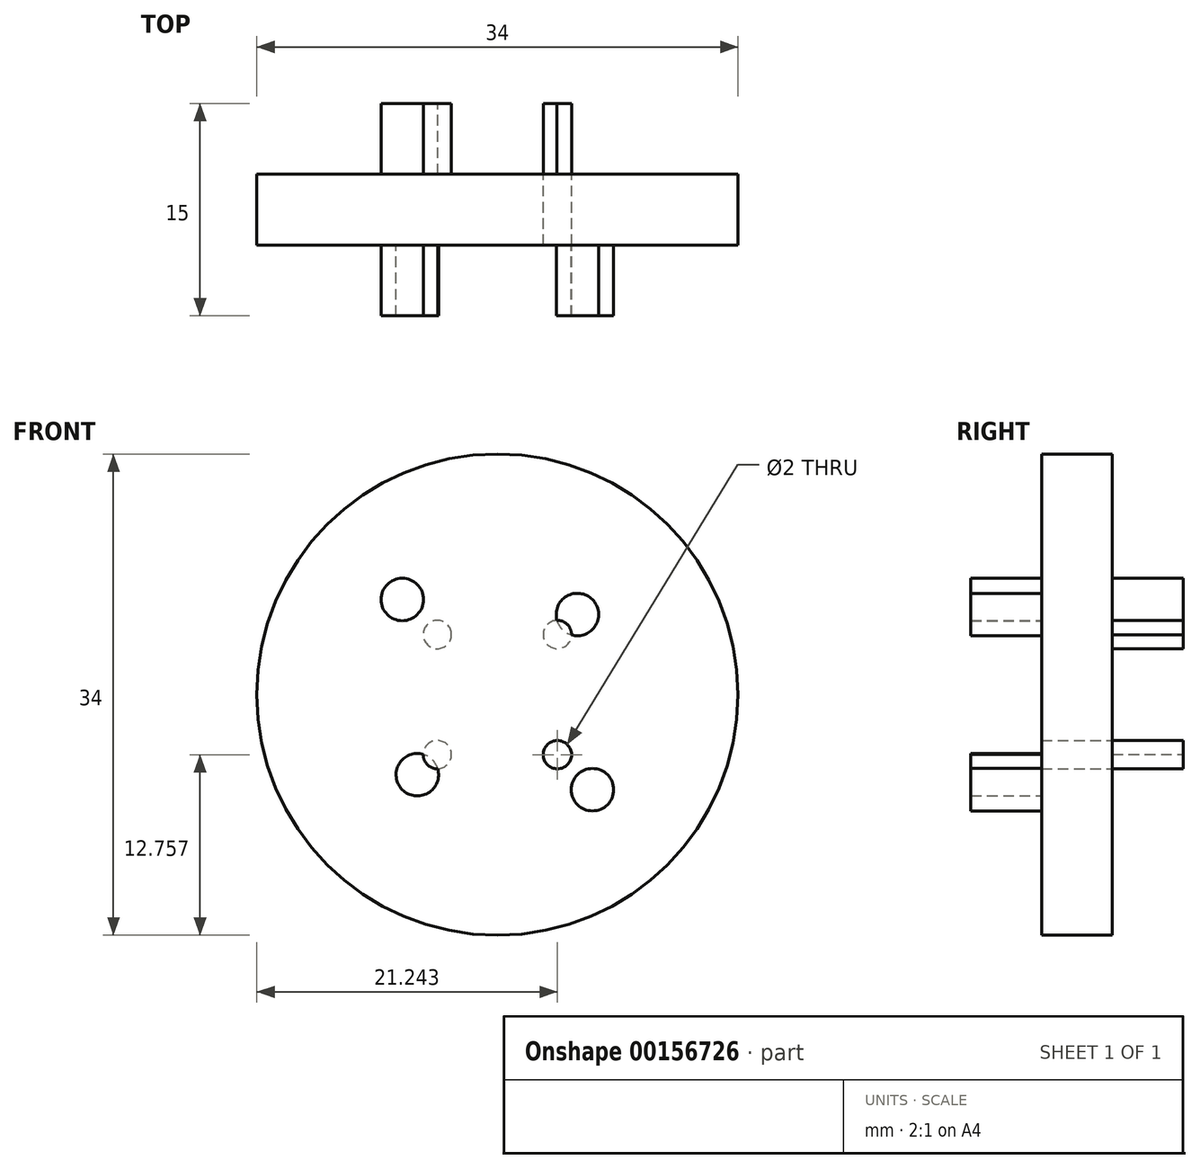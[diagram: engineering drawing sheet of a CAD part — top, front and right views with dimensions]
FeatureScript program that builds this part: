
annotation { "Feature Type Name" : "Feature", "Feature Type Description" : "" }
export const myFeature = defineFeature(function(context is Context, id is Id, definition is map)
    precondition{}
    {
        {
            var Q0;
            Q0=qCreatedBy(makeId("Front.planeOp"),FACE);
            var sketch = newSketch(context, id + "F0", { "sketchPlane" : qUnion([Q0])});
            skCircle(sketch, "E0", {"center": v(0, 0) * mm, "radius": 17 * mm});
            skCircle(sketch, "E1", {"center": v(5.66, 5.66) * mm, "radius": 1.5 * mm});
            skCircle(sketch, "E2.MirrorC", {"center": v(-6.72, 6.72) * mm, "radius": 1.5 * mm});
            skCircle(sketch, "E3.MirrorC", {"center": v(-5.66, -5.66) * mm, "radius": 1.5 * mm});
            skLineSegment(sketch, "E4", {"start": v(0, 29.65) * mm, "end": v(0, -28.8) * mm, "construction": true});
            skLineSegment(sketch, "E5", {"start": v(-6.72, 6.72) * mm, "end": v(4.6, -4.6) * mm, "construction": true});
            skLineSegment(sketch, "E6", {"start": v(5.66, 5.66) * mm, "end": v(-5.66, -5.66) * mm, "construction": true});
            skCircle(sketch, "E7", {"center": v(-4.24, 4.24) * mm, "radius": 1 * mm});
            skCircle(sketch, "E8.MirrorC", {"center": v(4.24, 4.24) * mm, "radius": 1 * mm});
            skCircle(sketch, "E9.MirrorC", {"center": v(4.24, -4.24) * mm, "radius": 1 * mm});
            skCircle(sketch, "E10.MirrorC", {"center": v(-4.24, -4.24) * mm, "radius": 1 * mm});
            skCircle(sketch, "E11.MirrorC", {"center": v(6.72, -6.72) * mm, "radius": 1.5 * mm});
            skSolve(sketch);
        }
        {
            var Q0;
            Q0=makeQuery(id+"F0.imprint","IMPRINT",FACE,{"disambiguationData":[TD([[makeQuery(id+"F0.imprint","IMPRINT",EDGE,{"derivedFrom":sQuery(id+"F0.wireOp",EDGE,"E0")}),1.0]])]});
            var Q1;
            {var subQ0=sQuery(id+"F0.wireOp",EDGE,"E7");var subQ1=sQuery(id+"F0.wireOp",EDGE,"E2.MirrorC");var subQ2=makeQuery(id+"F0.imprint","INTERSECT",VERTEX,{"disambiguationData":[OD(0.0)],"derivedFrom":[subQ1,subQ0]});Q1=makeQuery(id+"F0.imprint","IMPRINT",FACE,{"disambiguationData":[TD([[makeQuery(id+"F0.imprint","IMPRINT",EDGE,{"disambiguationData":[TD([[subQ2,-1.0]])],"derivedFrom":subQ1}),-1.0]])]});}
            var Q2;
            {var subQ0=sQuery(id+"F0.wireOp",EDGE,"E8.MirrorC");var subQ1=sQuery(id+"F0.wireOp",EDGE,"E1");var subQ2=makeQuery(id+"F0.imprint","INTERSECT",VERTEX,{"disambiguationData":[OD(0.0)],"derivedFrom":[subQ1,subQ0]});Q2=makeQuery(id+"F0.imprint","IMPRINT",FACE,{"disambiguationData":[TD([[makeQuery(id+"F0.imprint","IMPRINT",EDGE,{"disambiguationData":[TD([[subQ2,1.0]])],"derivedFrom":subQ1}),1.0]])]});}
            var Q3;
            {var subQ0=sQuery(id+"F0.wireOp",EDGE,"E8.MirrorC");var subQ1=sQuery(id+"F0.wireOp",EDGE,"E1");var subQ2=makeQuery(id+"F0.imprint","INTERSECT",VERTEX,{"disambiguationData":[OD(0.0)],"derivedFrom":[subQ1,subQ0]});Q3=makeQuery(id+"F0.imprint","IMPRINT",FACE,{"disambiguationData":[TD([[makeQuery(id+"F0.imprint","IMPRINT",EDGE,{"disambiguationData":[TD([[subQ2,-1.0]])],"derivedFrom":subQ1}),-1.0]])]});}
            var Q4;
            {var subQ0=sQuery(id+"F0.wireOp",EDGE,"E7");var subQ1=sQuery(id+"F0.wireOp",EDGE,"E2.MirrorC");var subQ2=makeQuery(id+"F0.imprint","INTERSECT",VERTEX,{"disambiguationData":[OD(0.0)],"derivedFrom":[subQ1,subQ0]});Q4=makeQuery(id+"F0.imprint","IMPRINT",FACE,{"disambiguationData":[TD([[makeQuery(id+"F0.imprint","IMPRINT",EDGE,{"disambiguationData":[TD([[subQ2,1.0]])],"derivedFrom":subQ1}),-1.0]])]});}
            var Q5;
            {var subQ0=sQuery(id+"F0.wireOp",EDGE,"E7");var subQ1=sQuery(id+"F0.wireOp",EDGE,"E2.MirrorC");var subQ2=makeQuery(id+"F0.imprint","INTERSECT",VERTEX,{"disambiguationData":[OD(0.0)],"derivedFrom":[subQ1,subQ0]});Q5=makeQuery(id+"F0.imprint","IMPRINT",FACE,{"disambiguationData":[TD([[makeQuery(id+"F0.imprint","IMPRINT",EDGE,{"disambiguationData":[TD([[subQ2,1.0]])],"derivedFrom":subQ1}),1.0]])]});}
            var Q6;
            {var subQ0=sQuery(id+"F0.wireOp",EDGE,"E10.MirrorC");var subQ1=sQuery(id+"F0.wireOp",EDGE,"E3.MirrorC");var subQ2=makeQuery(id+"F0.imprint","INTERSECT",VERTEX,{"disambiguationData":[OD(0.0)],"derivedFrom":[subQ1,subQ0]});Q6=makeQuery(id+"F0.imprint","IMPRINT",FACE,{"disambiguationData":[TD([[makeQuery(id+"F0.imprint","IMPRINT",EDGE,{"disambiguationData":[TD([[subQ2,-1.0]])],"derivedFrom":subQ1}),1.0]])]});}
            var Q7;
            {var subQ0=sQuery(id+"F0.wireOp",EDGE,"E10.MirrorC");var subQ1=sQuery(id+"F0.wireOp",EDGE,"E3.MirrorC");var subQ2=makeQuery(id+"F0.imprint","INTERSECT",VERTEX,{"disambiguationData":[OD(0.0)],"derivedFrom":[subQ1,subQ0]});Q7=makeQuery(id+"F0.imprint","IMPRINT",FACE,{"disambiguationData":[TD([[makeQuery(id+"F0.imprint","IMPRINT",EDGE,{"disambiguationData":[TD([[subQ2,1.0]])],"derivedFrom":subQ1}),1.0]])]});}
            var Q8;
            {var subQ0=sQuery(id+"F0.wireOp",EDGE,"E10.MirrorC");var subQ1=sQuery(id+"F0.wireOp",EDGE,"E3.MirrorC");var subQ2=makeQuery(id+"F0.imprint","INTERSECT",VERTEX,{"disambiguationData":[OD(0.0)],"derivedFrom":[subQ1,subQ0]});Q8=makeQuery(id+"F0.imprint","IMPRINT",FACE,{"disambiguationData":[TD([[makeQuery(id+"F0.imprint","IMPRINT",EDGE,{"disambiguationData":[TD([[subQ2,1.0]])],"derivedFrom":subQ1}),-1.0]])]});}
            var Q9;
            {var subQ0=sQuery(id+"F0.wireOp",EDGE,"E8.MirrorC");var subQ1=sQuery(id+"F0.wireOp",EDGE,"E1");var subQ2=makeQuery(id+"F0.imprint","INTERSECT",VERTEX,{"disambiguationData":[OD(0.0)],"derivedFrom":[subQ1,subQ0]});Q9=makeQuery(id+"F0.imprint","IMPRINT",FACE,{"disambiguationData":[TD([[makeQuery(id+"F0.imprint","IMPRINT",EDGE,{"disambiguationData":[TD([[subQ2,-1.0]])],"derivedFrom":subQ1}),1.0]])]});}
            var Q10;
            {var subQ0=sQuery(id+"F0.wireOp",EDGE,"E9.MirrorC");var subQ1=sQuery(id+"F0.wireOp",EDGE,"ca95e133-498b-419e-b427-ecf875a2ec590.MirrorC");var subQ2=makeQuery(id+"F0.imprint","INTERSECT",VERTEX,{"disambiguationData":[OD(0.0)],"derivedFrom":[subQ1,subQ0]});Q10=makeQuery(id+"F0.imprint","IMPRINT",FACE,{"disambiguationData":[TD([[makeQuery(id+"F0.imprint","IMPRINT",EDGE,{"disambiguationData":[TD([[subQ2,-1.0]])],"derivedFrom":subQ1}),1.0]])]});}
            var Q11;
            {var subQ0=sQuery(id+"F0.wireOp",EDGE,"E9.MirrorC");var subQ1=sQuery(id+"F0.wireOp",EDGE,"ca95e133-498b-419e-b427-ecf875a2ec590.MirrorC");var subQ2=makeQuery(id+"F0.imprint","INTERSECT",VERTEX,{"disambiguationData":[OD(0.0)],"derivedFrom":[subQ1,subQ0]});Q11=makeQuery(id+"F0.imprint","IMPRINT",FACE,{"disambiguationData":[TD([[makeQuery(id+"F0.imprint","IMPRINT",EDGE,{"disambiguationData":[TD([[subQ2,-1.0]])],"derivedFrom":subQ1}),-1.0]])]});}
            var Q12;
            {var subQ0=sQuery(id+"F0.wireOp",EDGE,"E9.MirrorC");var subQ1=sQuery(id+"F0.wireOp",EDGE,"ca95e133-498b-419e-b427-ecf875a2ec590.MirrorC");var subQ2=makeQuery(id+"F0.imprint","INTERSECT",VERTEX,{"disambiguationData":[OD(0.0)],"derivedFrom":[subQ1,subQ0]});Q12=makeQuery(id+"F0.imprint","IMPRINT",FACE,{"disambiguationData":[TD([[makeQuery(id+"F0.imprint","IMPRINT",EDGE,{"disambiguationData":[TD([[subQ2,1.0]])],"derivedFrom":subQ1}),-1.0]])]});}
            var Q13;
            Q13=makeQuery(id+"F0.imprint","IMPRINT",FACE,{"disambiguationData":[TD([[makeQuery(id+"F0.imprint","IMPRINT",EDGE,{"derivedFrom":sQuery(id+"F0.wireOp",EDGE,"E9.MirrorC")}),-1.0]])]});
            var Q14;
            Q14=makeQuery(id+"F0.imprint","IMPRINT",FACE,{"disambiguationData":[TD([[makeQuery(id+"F0.imprint","IMPRINT",EDGE,{"derivedFrom":sQuery(id+"F0.wireOp",EDGE,"E7")}),1.0]])]});
            var Q15;
            Q15=makeQuery(id+"F0.imprint","IMPRINT",FACE,{"disambiguationData":[TD([[makeQuery(id+"F0.imprint","IMPRINT",EDGE,{"derivedFrom":sQuery(id+"F0.wireOp",EDGE,"E2.MirrorC")}),-1.0]])]});
            var Q16;
            Q16=makeQuery(id+"F0.imprint","IMPRINT",FACE,{"disambiguationData":[TD([[makeQuery(id+"F0.imprint","IMPRINT",EDGE,{"derivedFrom":sQuery(id+"F0.wireOp",EDGE,"E11.MirrorC")}),1.0]])]});
            extrude(context, id + "F1", {"entities" : qUnion([Q0, Q1, Q2, Q3, Q4, Q5, Q6, Q7, Q8, Q9, Q10, Q11, Q12, Q13, Q14, Q15, Q16]), "depth" : 15 * mm});
        }
        {
            var Q0;
            {var subQ0=sQuery(id+"F0.wireOp",EDGE,"E10.MirrorC");var subQ1=sQuery(id+"F0.wireOp",EDGE,"E3.MirrorC");var subQ2=makeQuery(id+"F0.imprint","INTERSECT",VERTEX,{"disambiguationData":[OD(0.0)],"derivedFrom":[subQ1,subQ0]});Q0=makeQuery(id+"F0.imprint","IMPRINT",FACE,{"disambiguationData":[TD([[makeQuery(id+"F0.imprint","IMPRINT",EDGE,{"disambiguationData":[TD([[subQ2,1.0]])],"derivedFrom":subQ1}),-1.0]])]});}
            var Q1;
            {var subQ0=sQuery(id+"F0.wireOp",EDGE,"E10.MirrorC");var subQ1=sQuery(id+"F0.wireOp",EDGE,"E3.MirrorC");var subQ2=makeQuery(id+"F0.imprint","INTERSECT",VERTEX,{"disambiguationData":[OD(0.0)],"derivedFrom":[subQ1,subQ0]});Q1=makeQuery(id+"F0.imprint","IMPRINT",FACE,{"disambiguationData":[TD([[makeQuery(id+"F0.imprint","IMPRINT",EDGE,{"disambiguationData":[TD([[subQ2,1.0]])],"derivedFrom":subQ1}),1.0]])]});}
            var Q2;
            Q2=makeQuery(id+"F0.imprint","IMPRINT",FACE,{"disambiguationData":[TD([[makeQuery(id+"F0.imprint","IMPRINT",EDGE,{"derivedFrom":sQuery(id+"F0.wireOp",EDGE,"E9.MirrorC")}),-1.0]])]});
            var Q3;
            {var subQ0=sQuery(id+"F0.wireOp",EDGE,"E8.MirrorC");var subQ1=sQuery(id+"F0.wireOp",EDGE,"E1");var subQ2=makeQuery(id+"F0.imprint","INTERSECT",VERTEX,{"disambiguationData":[OD(0.0)],"derivedFrom":[subQ1,subQ0]});Q3=makeQuery(id+"F0.imprint","IMPRINT",FACE,{"disambiguationData":[TD([[makeQuery(id+"F0.imprint","IMPRINT",EDGE,{"disambiguationData":[TD([[subQ2,-1.0]])],"derivedFrom":subQ1}),-1.0]])]});}
            var Q4;
            {var subQ0=sQuery(id+"F0.wireOp",EDGE,"E8.MirrorC");var subQ1=sQuery(id+"F0.wireOp",EDGE,"E1");var subQ2=makeQuery(id+"F0.imprint","INTERSECT",VERTEX,{"disambiguationData":[OD(0.0)],"derivedFrom":[subQ1,subQ0]});Q4=makeQuery(id+"F0.imprint","IMPRINT",FACE,{"disambiguationData":[TD([[makeQuery(id+"F0.imprint","IMPRINT",EDGE,{"disambiguationData":[TD([[subQ2,-1.0]])],"derivedFrom":subQ1}),1.0]])]});}
            var Q5;
            Q5=makeQuery(id+"F0.imprint","IMPRINT",FACE,{"disambiguationData":[TD([[makeQuery(id+"F0.imprint","IMPRINT",EDGE,{"derivedFrom":sQuery(id+"F0.wireOp",EDGE,"E7")}),1.0]])]});
            extrude(context, id + "F2", {"entities" : qUnion([Q0, Q1, Q2, Q3, Q4, Q5]), "operationType" : NewBodyOperationType.REMOVE, "depth" : 25 * mm, "hasSecondDirection" : true, "secondDirectionOppositeDirection" : false, "secondDirectionDepth" : 10 * mm});
        }
        {
            var Q0;
            {var subQ0=sQuery(id+"F0.wireOp",EDGE,"E7");var subQ1=sQuery(id+"F0.wireOp",EDGE,"E2.MirrorC");var subQ2=makeQuery(id+"F0.imprint","INTERSECT",VERTEX,{"disambiguationData":[OD(0.0)],"derivedFrom":[subQ1,subQ0]});Q0=makeQuery(id+"F0.imprint","IMPRINT",FACE,{"disambiguationData":[TD([[makeQuery(id+"F0.imprint","IMPRINT",EDGE,{"disambiguationData":[TD([[subQ2,-1.0]])],"derivedFrom":subQ1}),-1.0]])]});}
            var Q1;
            {var subQ0=sQuery(id+"F0.wireOp",EDGE,"E7");var subQ1=sQuery(id+"F0.wireOp",EDGE,"E2.MirrorC");var subQ2=makeQuery(id+"F0.imprint","INTERSECT",VERTEX,{"disambiguationData":[OD(0.0)],"derivedFrom":[subQ1,subQ0]});Q1=makeQuery(id+"F0.imprint","IMPRINT",FACE,{"disambiguationData":[TD([[makeQuery(id+"F0.imprint","IMPRINT",EDGE,{"disambiguationData":[TD([[subQ2,1.0]])],"derivedFrom":subQ1}),-1.0]])]});}
            var Q2;
            {var subQ0=sQuery(id+"F0.wireOp",EDGE,"E8.MirrorC");var subQ1=sQuery(id+"F0.wireOp",EDGE,"E1");var subQ2=makeQuery(id+"F0.imprint","INTERSECT",VERTEX,{"disambiguationData":[OD(0.0)],"derivedFrom":[subQ1,subQ0]});Q2=makeQuery(id+"F0.imprint","IMPRINT",FACE,{"disambiguationData":[TD([[makeQuery(id+"F0.imprint","IMPRINT",EDGE,{"disambiguationData":[TD([[subQ2,1.0]])],"derivedFrom":subQ1}),1.0]])]});}
            var Q3;
            {var subQ0=sQuery(id+"F0.wireOp",EDGE,"E8.MirrorC");var subQ1=sQuery(id+"F0.wireOp",EDGE,"E1");var subQ2=makeQuery(id+"F0.imprint","INTERSECT",VERTEX,{"disambiguationData":[OD(0.0)],"derivedFrom":[subQ1,subQ0]});Q3=makeQuery(id+"F0.imprint","IMPRINT",FACE,{"disambiguationData":[TD([[makeQuery(id+"F0.imprint","IMPRINT",EDGE,{"disambiguationData":[TD([[subQ2,-1.0]])],"derivedFrom":subQ1}),1.0]])]});}
            var Q4;
            {var subQ0=sQuery(id+"F0.wireOp",EDGE,"E9.MirrorC");var subQ1=sQuery(id+"F0.wireOp",EDGE,"ca95e133-498b-419e-b427-ecf875a2ec590.MirrorC");var subQ2=makeQuery(id+"F0.imprint","INTERSECT",VERTEX,{"disambiguationData":[OD(0.0)],"derivedFrom":[subQ1,subQ0]});Q4=makeQuery(id+"F0.imprint","IMPRINT",FACE,{"disambiguationData":[TD([[makeQuery(id+"F0.imprint","IMPRINT",EDGE,{"disambiguationData":[TD([[subQ2,1.0]])],"derivedFrom":subQ1}),-1.0]])]});}
            var Q5;
            {var subQ0=sQuery(id+"F0.wireOp",EDGE,"E9.MirrorC");var subQ1=sQuery(id+"F0.wireOp",EDGE,"ca95e133-498b-419e-b427-ecf875a2ec590.MirrorC");var subQ2=makeQuery(id+"F0.imprint","INTERSECT",VERTEX,{"disambiguationData":[OD(0.0)],"derivedFrom":[subQ1,subQ0]});Q5=makeQuery(id+"F0.imprint","IMPRINT",FACE,{"disambiguationData":[TD([[makeQuery(id+"F0.imprint","IMPRINT",EDGE,{"disambiguationData":[TD([[subQ2,-1.0]])],"derivedFrom":subQ1}),-1.0]])]});}
            var Q6;
            {var subQ0=sQuery(id+"F0.wireOp",EDGE,"E10.MirrorC");var subQ1=sQuery(id+"F0.wireOp",EDGE,"E3.MirrorC");var subQ2=makeQuery(id+"F0.imprint","INTERSECT",VERTEX,{"disambiguationData":[OD(0.0)],"derivedFrom":[subQ1,subQ0]});Q6=makeQuery(id+"F0.imprint","IMPRINT",FACE,{"disambiguationData":[TD([[makeQuery(id+"F0.imprint","IMPRINT",EDGE,{"disambiguationData":[TD([[subQ2,-1.0]])],"derivedFrom":subQ1}),1.0]])]});}
            var Q7;
            {var subQ0=sQuery(id+"F0.wireOp",EDGE,"E10.MirrorC");var subQ1=sQuery(id+"F0.wireOp",EDGE,"E3.MirrorC");var subQ2=makeQuery(id+"F0.imprint","INTERSECT",VERTEX,{"disambiguationData":[OD(0.0)],"derivedFrom":[subQ1,subQ0]});Q7=makeQuery(id+"F0.imprint","IMPRINT",FACE,{"disambiguationData":[TD([[makeQuery(id+"F0.imprint","IMPRINT",EDGE,{"disambiguationData":[TD([[subQ2,1.0]])],"derivedFrom":subQ1}),1.0]])]});}
            var Q8;
            Q8=makeQuery(id+"F0.imprint","IMPRINT",FACE,{"disambiguationData":[TD([[makeQuery(id+"F0.imprint","IMPRINT",EDGE,{"derivedFrom":sQuery(id+"F0.wireOp",EDGE,"E11.MirrorC")}),1.0]])]});
            var Q9;
            Q9=makeQuery(id+"F0.imprint","IMPRINT",FACE,{"disambiguationData":[TD([[makeQuery(id+"F0.imprint","IMPRINT",EDGE,{"derivedFrom":sQuery(id+"F0.wireOp",EDGE,"E2.MirrorC")}),-1.0]])]});
            extrude(context, id + "F3", {"entities" : qUnion([Q0, Q1, Q2, Q3, Q4, Q5, Q6, Q7, Q8, Q9]), "operationType" : NewBodyOperationType.REMOVE, "depth" : 5 * mm});
        }
    });
